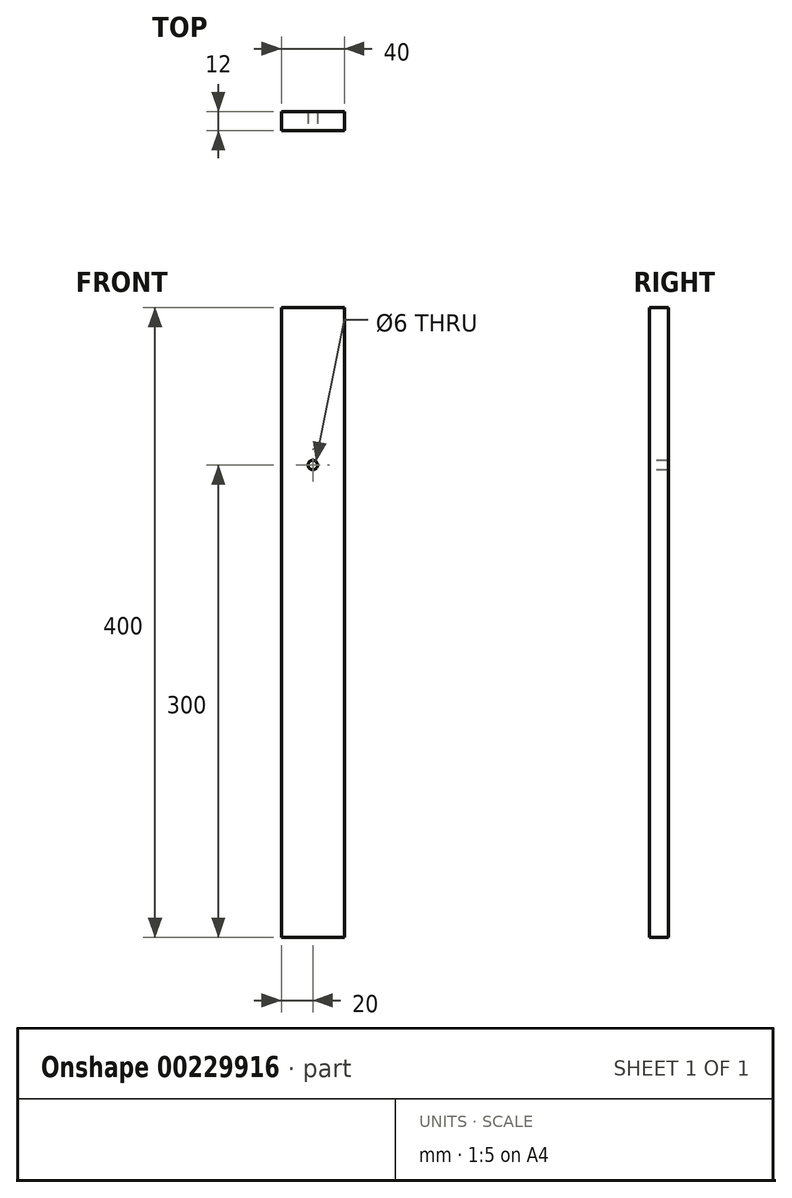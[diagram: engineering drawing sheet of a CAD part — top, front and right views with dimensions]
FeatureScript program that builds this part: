
annotation { "Feature Type Name" : "Feature", "Feature Type Description" : "" }
export const myFeature = defineFeature(function(context is Context, id is Id, definition is map)
    precondition{}
    {
        {
            var Q0;
            Q0=qCreatedBy(makeId("Top.planeOp"),FACE);
            var sketch = newSketch(context, id + "F0", { "sketchPlane" : qUnion([Q0])});
            skLineSegment(sketch, "E0.bottom", {"start": v(0, 0) * mm, "end": v(40, 0) * mm});
            skLineSegment(sketch, "E0.top", {"start": v(0, 12) * mm, "end": v(40, 12) * mm});
            skLineSegment(sketch, "E0.left", {"start": v(0, 0) * mm, "end": v(0, 12) * mm});
            skLineSegment(sketch, "E0.right", {"start": v(40, 0) * mm, "end": v(40, 12) * mm});
            skSolve(sketch);
        }
        {
            var Q0;
            Q0=qSketchRegion(id+"F0",true);
            extrude(context, id + "F1", {"entities" : qUnion([Q0]), "depth" : 400 * mm});
        }
        {
            var Q0;
            Q0=makeQuery(id+"F1.opExtrude","SWEPT_FACE",FACE,{"disambiguationData":[OSD([sQuery(id+"F0.wireOp",EDGE,"E0.bottom")])]});
            var sketch = newSketch(context, id + "F2", { "sketchPlane" : qUnion([Q0])});
            skCircle(sketch, "E1", {"center": v(20, 300) * mm, "radius": 8.42 * mm});
            skSolve(sketch);
        }
        {
            var Q0;
            Q0=sQuery(id+"F2.wireOp",VERTEX,"E1.center");
            var Q1;
            Q1=makeQuery(id+"F1.opExtrude","SWEPT_BODY",BODY,{"disambiguationData":[OSD([sQuery(id+"F0.wireOp",EDGE,"E0.bottom"),sQuery(id+"F0.wireOp",EDGE,"E0.top"),sQuery(id+"F0.wireOp",EDGE,"E0.left"),sQuery(id+"F0.wireOp",EDGE,"E0.right")])]});
            hole(context, id + "F3", {"style" : HoleStyle.SIMPLE, "endStyle" : HoleEndStyle.THROUGH, "holeDiameter" : 6 * mm, "locations" : qUnion([Q0]), "scope" : qUnion([Q1]), "isTappedThrough" : true});
        }
    });
